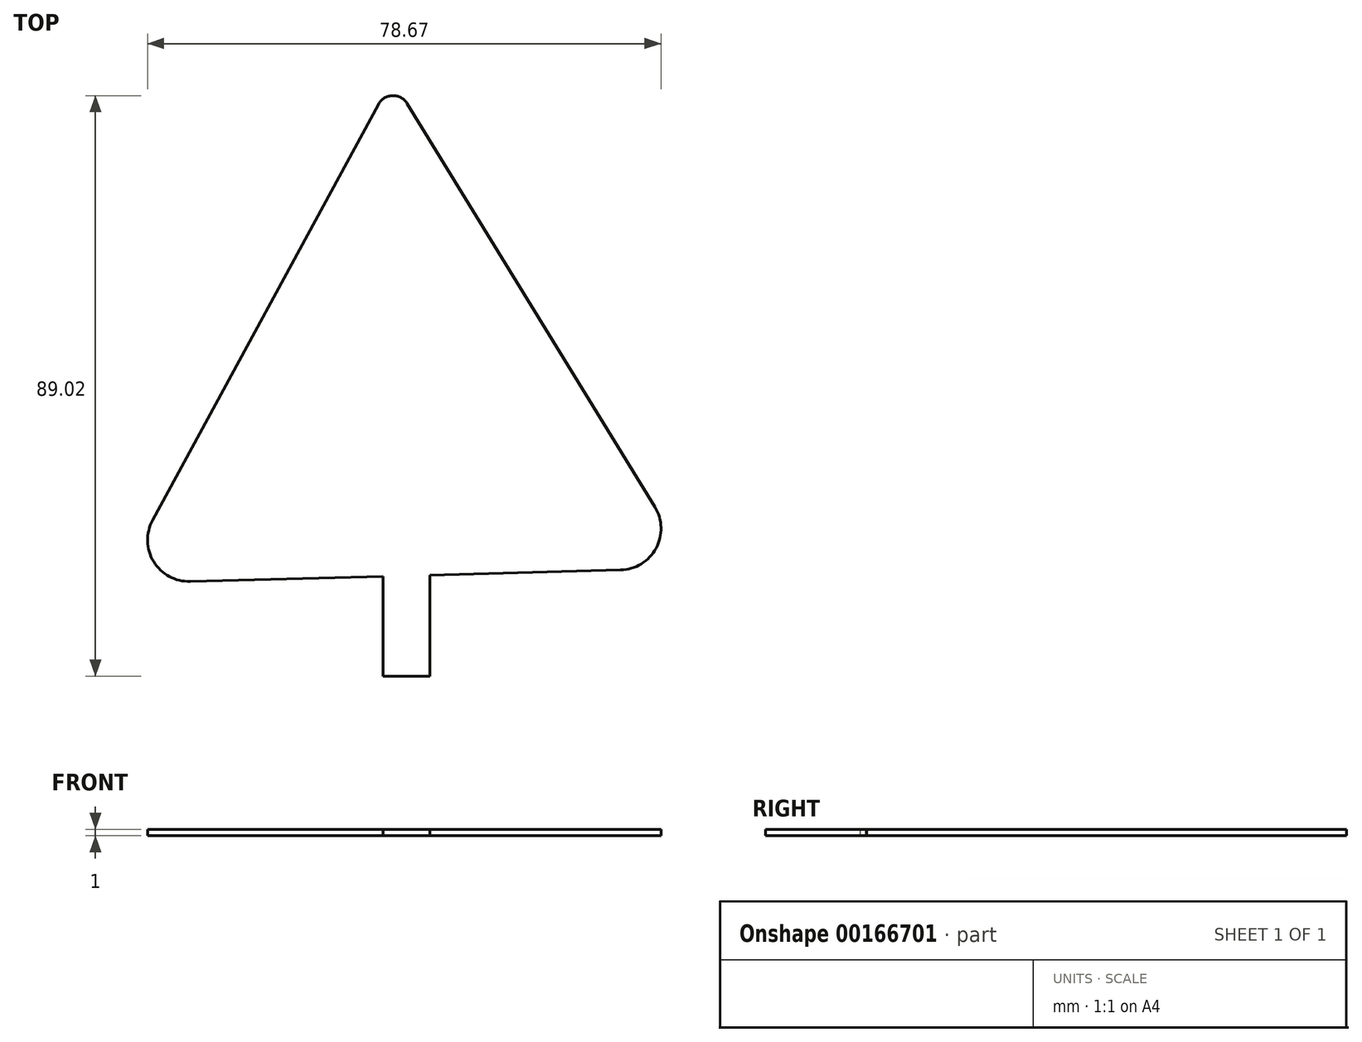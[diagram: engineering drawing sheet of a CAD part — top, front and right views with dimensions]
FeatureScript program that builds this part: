
annotation { "Feature Type Name" : "Feature", "Feature Type Description" : "" }
export const myFeature = defineFeature(function(context is Context, id is Id, definition is map)
    precondition{}
    {
        {
            var Q0;
            Q0=qCreatedBy(makeId("Top.planeOp"),FACE);
            var sketch = newSketch(context, id + "F0", { "sketchPlane" : qUnion([Q0])});
            skCircle(sketch, "E0", {"center": v(0, 0) * mm, "radius": 25.4 * mm});
            skArc(sketch, "E1.cCircle", {"start": v(4.4, -25.02) * mm, "mid": v(20.61, 14.84) * mm, "end": v(-22.33, 12.1) * mm, "construction": true});
            skLineSegment(sketch, "E1.0", {"start": v(0.95, 47.03) * mm, "end": v(38.9, -14.84) * mm});
            skLineSegment(sketch, "E1.1", {"start": v(33.66, -24.51) * mm, "end": v(4.4, -25.3) * mm});
            skLineSegment(sketch, "E1.2", {"start": v(-38.06, -16.9) * mm, "end": v(-3.45, 46.91) * mm});
            skPoint(sketch, "E1.0.midPoint", {"position": v(21.65, 13.28) * mm});
            skPoint(sketch, "E2.visualSharp", {"position": v(-43.3, -26.56) * mm});
            skArc(sketch, "E2.filletArc", {"start": v(-38.06, -16.9) * mm, "mid": v(-37.89, -23.24) * mm, "end": v(-32.3, -26.27) * mm});
            skPoint(sketch, "E3.visualSharp", {"position": v(44.66, -24.22) * mm});
            skArc(sketch, "E3.filletArc", {"start": v(33.66, -24.51) * mm, "mid": v(39.07, -21.2) * mm, "end": v(38.9, -14.84) * mm});
            skPoint(sketch, "E4.visualSharp", {"position": v(-1.35, 50.78) * mm});
            skArc(sketch, "E4.filletArc", {"start": v(0.95, 47.03) * mm, "mid": v(-1.29, 48.24) * mm, "end": v(-3.45, 46.91) * mm});
            skLineSegment(sketch, "E5.top", {"start": v(-2.75, -40.78) * mm, "end": v(4.4, -40.78) * mm});
            skLineSegment(sketch, "E5.left", {"start": v(-2.75, -25.25) * mm, "end": v(-2.75, -40.78) * mm});
            skLineSegment(sketch, "E5.right", {"start": v(4.4, -25.02) * mm, "end": v(4.4, -40.78) * mm});
            skLineSegment(sketch, "E6.trimOffspring", {"start": v(-2.75, -25.48) * mm, "end": v(-32.3, -26.27) * mm});
            skSolve(sketch);
        }
        {
            var Q0;
            Q0=makeQuery(id+"F0.imprint","IMPRINT",FACE,{"disambiguationData":[TD([[makeQuery(id+"F0.imprint","IMPRINT",EDGE,{"derivedFrom":sQuery(id+"F0.wireOp",EDGE,"bdSfl7eX-f22n-R6Yx-E8Bb-wxDQlUoLlHQS.bottom")}),-1.0]])]});
            var Q1;
            {var subQ0=sQuery(id+"F0.wireOp",EDGE,"E2.filletArc");Q1=makeQuery(id+"F0.imprint","IMPRINT",FACE,{"disambiguationData":[TD([[makeQuery(id+"F0.imprint","IMPRINT",EDGE,{"derivedFrom":subQ0}),1.0]])]});}
            var Q2;
            {var subQ5=sQuery(id+"F0.wireOp",EDGE,"E3.filletArc");Q2=makeQuery(id+"F0.imprint","IMPRINT",FACE,{"disambiguationData":[TD([[makeQuery(id+"F0.imprint","IMPRINT",EDGE,{"derivedFrom":subQ5}),1.0]])]});}
            var Q3;
            {var subQ0=sQuery(id+"F0.wireOp",EDGE,"E0");var subQ1=makeQuery(id+"F0.imprint","INTERSECT",VERTEX,{"derivedFrom":[subQ0,sQuery(id+"F0.wireOp",EDGE,"E1.2")]});Q3=makeQuery(id+"F0.imprint","IMPRINT",FACE,{"disambiguationData":[TD([[makeQuery(id+"F0.imprint","IMPRINT",EDGE,{"disambiguationData":[TD([[subQ1,1.0]])],"derivedFrom":subQ0}),1.0]])]});}
            var Q4;
            {var subQ5=sQuery(id+"F0.wireOp",EDGE,"E4.filletArc");Q4=makeQuery(id+"F0.imprint","IMPRINT",FACE,{"disambiguationData":[TD([[makeQuery(id+"F0.imprint","IMPRINT",EDGE,{"derivedFrom":subQ5}),1.0]])]});}
            var Q5;
            {var subQ1=sQuery(id+"F0.wireOp",EDGE,"E5.top");Q5=makeQuery(id+"F0.imprint","IMPRINT",FACE,{"disambiguationData":[TD([[makeQuery(id+"F0.imprint","IMPRINT",EDGE,{"derivedFrom":subQ1}),1.0]])]});}
            extrude(context, id + "F1", {"entities" : qUnion([Q0, Q1, Q2, Q3, Q4, Q5]), "depth" : 1 * mm});
        }
    });
